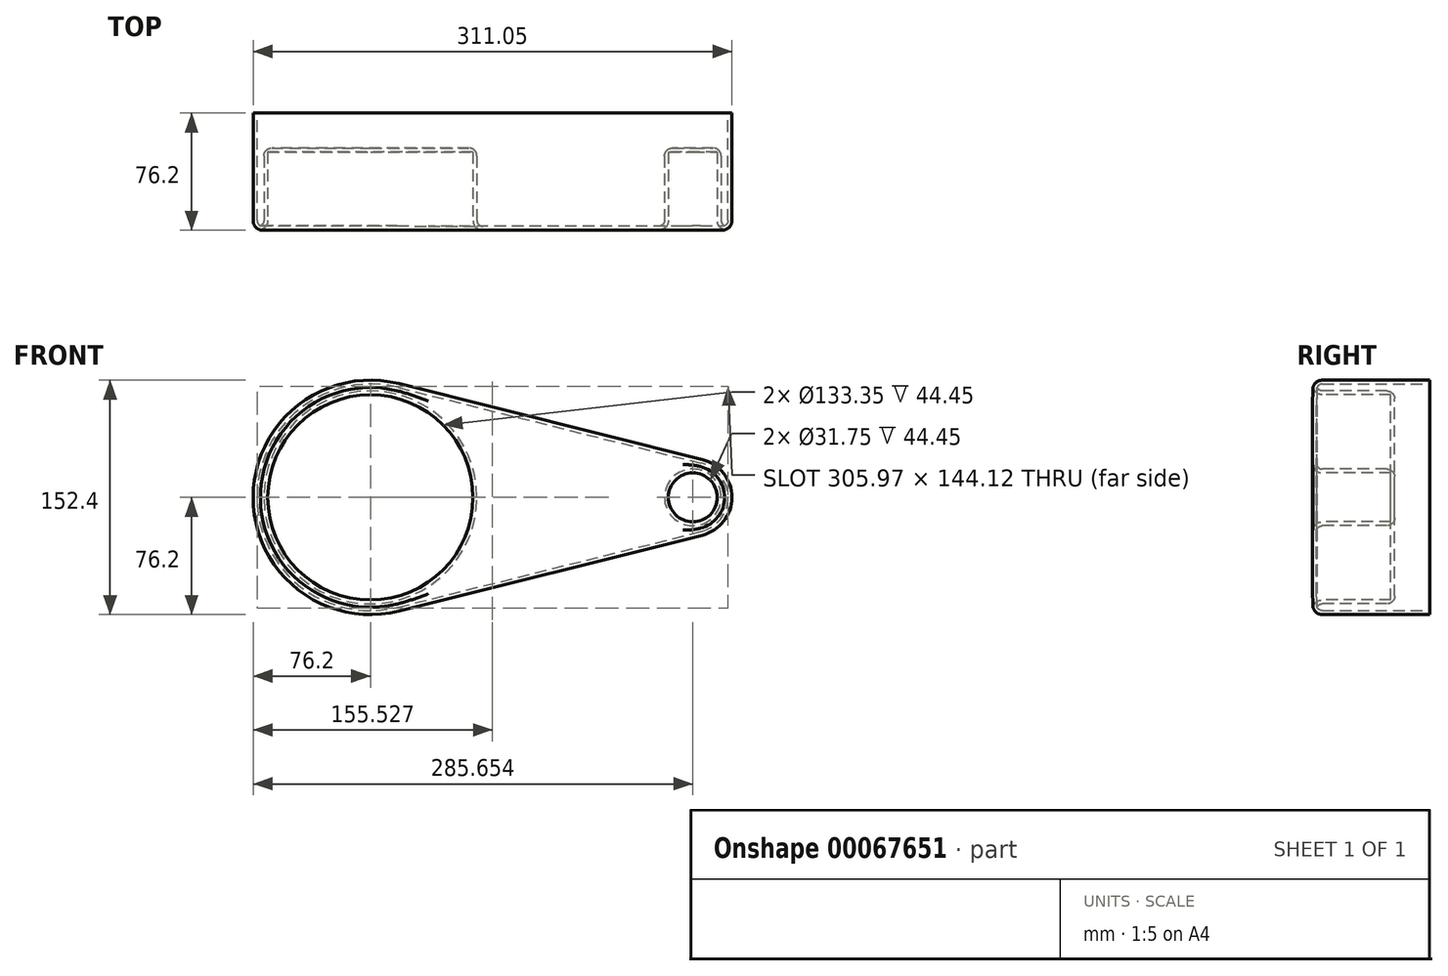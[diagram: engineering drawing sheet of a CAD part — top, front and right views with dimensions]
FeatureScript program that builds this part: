
annotation { "Feature Type Name" : "Feature", "Feature Type Description" : "" }
export const myFeature = defineFeature(function(context is Context, id is Id, definition is map)
    precondition{}
    {
        {
            var Q0;
            Q0=qCreatedBy(makeId("Front.planeOp"),FACE);
            var sketch = newSketch(context, id + "F0", { "sketchPlane" : qUnion([Q0])});
            skCircle(sketch, "E0", {"center": v(0, 0) * mm, "radius": 76.2 * mm});
            skCircle(sketch, "E1", {"center": v(209.45, 0) * mm, "radius": 25.4 * mm});
            skLineSegment(sketch, "E2", {"start": v(18.48, 73.92) * mm, "end": v(215.61, 24.64) * mm});
            skLineSegment(sketch, "E3", {"start": v(18.48, -73.92) * mm, "end": v(215.61, -24.64) * mm});
            skSolve(sketch);
        }
        {
            var Q0;
            {var subQ0=sQuery(id+"F0.wireOp",EDGE,"E1");var subQ1=makeQuery(id+"F0.imprint","INTERSECT",VERTEX,{"derivedFrom":[subQ0,sQuery(id+"F0.wireOp",EDGE,"E2")]});Q0=makeQuery(id+"F0.imprint","IMPRINT",FACE,{"disambiguationData":[TD([[makeQuery(id+"F0.imprint","IMPRINT",EDGE,{"disambiguationData":[TD([[subQ1,-1.0]])],"derivedFrom":subQ0}),1.0]])]});}
            var Q1;
            {var subQ0=sQuery(id+"F0.wireOp",EDGE,"E2");Q1=makeQuery(id+"F0.imprint","IMPRINT",FACE,{"disambiguationData":[TD([[makeQuery(id+"F0.imprint","IMPRINT",EDGE,{"derivedFrom":subQ0}),-1.0]])]});}
            var Q2;
            {var subQ0=sQuery(id+"F0.wireOp",EDGE,"E0");var subQ1=makeQuery(id+"F0.imprint","INTERSECT",VERTEX,{"derivedFrom":[subQ0,sQuery(id+"F0.wireOp",EDGE,"E2")]});Q2=makeQuery(id+"F0.imprint","IMPRINT",FACE,{"disambiguationData":[TD([[makeQuery(id+"F0.imprint","IMPRINT",EDGE,{"disambiguationData":[TD([[subQ1,-1.0]])],"derivedFrom":subQ0}),1.0]])]});}
            extrude(context, id + "F1", {"entities" : qUnion([Q0, Q1, Q2]), "depth" : 76.2 * mm});
        }
        {
            var Q0;
            Q0=makeQuery(id+"F1.opExtrude","CAP_FACE",FACE,{"disambiguationData":[OSD([sQuery(id+"F0.wireOp",EDGE,"E0"),sQuery(id+"F0.wireOp",EDGE,"E1"),sQuery(id+"F0.wireOp",EDGE,"E2"),sQuery(id+"F0.wireOp",EDGE,"E3")])],"isStart":false});
            var sketch = newSketch(context, id + "F2", { "sketchPlane" : qUnion([Q0])});
            skCircle(sketch, "E4", {"center": v(0, 0) * mm, "radius": 66.68 * mm});
            skCircle(sketch, "E5", {"center": v(209.45, 0) * mm, "radius": 15.88 * mm});
            skSolve(sketch);
        }
        {
            var Q0;
            Q0=makeQuery(id+"F2.imprint","IMPRINT",FACE,{"disambiguationData":[TD([[makeQuery(id+"F2.imprint","IMPRINT",EDGE,{"derivedFrom":sQuery(id+"F2.wireOp",EDGE,"E5")}),1.0]])]});
            var Q1;
            Q1=makeQuery(id+"F2.imprint","IMPRINT",FACE,{"disambiguationData":[TD([[makeQuery(id+"F2.imprint","IMPRINT",EDGE,{"derivedFrom":sQuery(id+"F2.wireOp",EDGE,"E4")}),1.0]])]});
            extrude(context, id + "F3", {"entities" : qUnion([Q0, Q1]), "operationType" : NewBodyOperationType.REMOVE, "oppositeDirection" : true, "depth" : 50.8 * mm});
        }
        {
            var Q0;
            Q0=makeQuery(id+"F1.opExtrude","CAP_FACE",FACE,{"disambiguationData":[OSD([sQuery(id+"F0.wireOp",EDGE,"E0"),sQuery(id+"F0.wireOp",EDGE,"E1"),sQuery(id+"F0.wireOp",EDGE,"E2"),sQuery(id+"F0.wireOp",EDGE,"E3")])],"isStart":false});
            fillet(context, id + "F4", {"entities" : qUnion([Q0]), "radius" : 6.35 * mm, "tangentPropagation" : true, "allowEdgeOverflow" : false});
        }
        {
            var Q0;
            Q0=makeQuery(id+"F1.opExtrude","CAP_FACE",FACE,{"disambiguationData":[OSD([sQuery(id+"F0.wireOp",EDGE,"E0"),sQuery(id+"F0.wireOp",EDGE,"E1"),sQuery(id+"F0.wireOp",EDGE,"E2"),sQuery(id+"F0.wireOp",EDGE,"E3")])],"isStart":true});
            shell(context, id + "F5", {"entities" : qUnion([Q0]), "thickness" : 2.54 * mm});
        }
        {
            var Q0;
            {var subQ0=sQuery(id+"F2.wireOp",EDGE,"E4");Q0=makeQuery(id+"F5.opShell","OFFSET_FACE",FACE,{"disambiguationData":[OSD([subQ0]),TDD([makeQuery(id+"F3.boolean.opBoolean","COPY",FACE,{"derivedFrom":makeQuery(id+"F3.opExtrude","CAP_FACE",FACE,{"disambiguationData":[OSD([subQ0])],"isStart":false})})])]});}
            var Q1;
            {var subQ0=sQuery(id+"F2.wireOp",EDGE,"E5");Q1=makeQuery(id+"F5.opShell","OFFSET_FACE",FACE,{"disambiguationData":[OSD([subQ0]),TDD([makeQuery(id+"F3.boolean.opBoolean","COPY",FACE,{"derivedFrom":makeQuery(id+"F3.opExtrude","CAP_FACE",FACE,{"disambiguationData":[OSD([subQ0])],"isStart":false})})])]});}
            fillet(context, id + "F6", {"entities" : qUnion([Q0, Q1]), "radius" : 5.08 * mm, "tangentPropagation" : true, "allowEdgeOverflow" : false});
        }
    });
